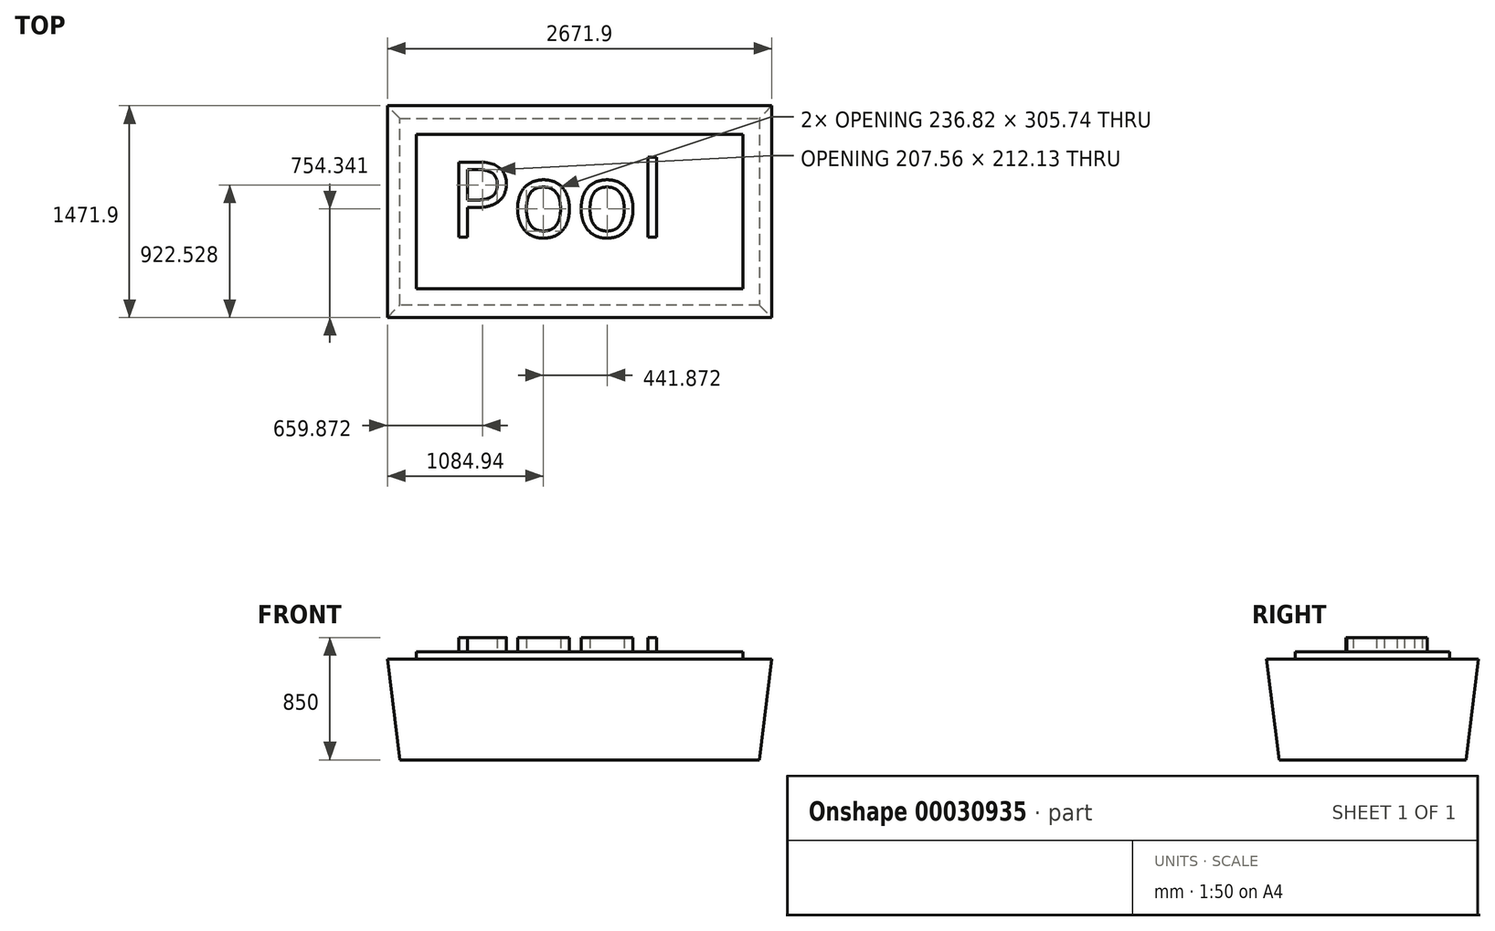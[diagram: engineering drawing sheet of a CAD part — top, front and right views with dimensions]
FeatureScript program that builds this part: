
annotation { "Feature Type Name" : "Feature", "Feature Type Description" : "" }
export const myFeature = defineFeature(function(context is Context, id is Id, definition is map)
    precondition{}
    {
        {
            var Q0;
            Q0=qCreatedBy(makeId("Top.planeOp"),FACE);
            var sketch = newSketch(context, id + "F0", { "sketchPlane" : qUnion([Q0])});
            skLineSegment(sketch, "E0.rect.bottom", {"start": v(-1250, 650) * mm, "end": v(1250, 650) * mm});
            skLineSegment(sketch, "E0.rect.top", {"start": v(-1250, -650) * mm, "end": v(1250, -650) * mm});
            skLineSegment(sketch, "E0.rect.left", {"start": v(-1250, 650) * mm, "end": v(-1250, -650) * mm});
            skLineSegment(sketch, "E0.rect.right", {"start": v(1250, 650) * mm, "end": v(1250, -650) * mm});
            skPoint(sketch, "E0.rect.middle", {"position": v(0, 0) * mm});
            skSolve(sketch);
        }
        {
            var Q0;
            Q0 = qSketchRegion(id + "F0", true);
            extrude(context, id + "F1", {"entities" : qUnion([Q0]), "depth" : 700 * mm, "hasDraft" : true, "draftAngle" : 7 * degree});
        }
        {
            var Q0;
            Q0=makeQuery(id+"F1.opExtrude","CAP_FACE",FACE,{"disambiguationData":[OSD([sQuery(id+"F0.wireOp",EDGE,"E0.rect.bottom"),sQuery(id+"F0.wireOp",EDGE,"E0.rect.top"),sQuery(id+"F0.wireOp",EDGE,"E0.rect.left"),sQuery(id+"F0.wireOp",EDGE,"E0.rect.right")])],"isStart":false});
            var sketch = newSketch(context, id + "F2", { "sketchPlane" : qUnion([Q0])});
            skLineSegment(sketch, "E1.rect.bottom", {"start": v(-1135.95, 535.95) * mm, "end": v(1135.95, 535.95) * mm});
            skLineSegment(sketch, "E1.rect.top", {"start": v(-1135.95, -535.95) * mm, "end": v(1135.95, -535.95) * mm});
            skLineSegment(sketch, "E1.rect.left", {"start": v(-1135.95, 535.95) * mm, "end": v(-1135.95, -535.95) * mm});
            skLineSegment(sketch, "E1.rect.right", {"start": v(1135.95, 535.95) * mm, "end": v(1135.95, -535.95) * mm});
            skPoint(sketch, "E1.rect.middle", {"position": v(0, 0) * mm});
            skSolve(sketch);
        }
        {
            var Q0;
            Q0 = qSketchRegion(id + "F2", true);
            extrude(context, id + "F3", {"entities" : qUnion([Q0]), "depth" : 50 * mm});
        }
        {
            var Q0;
            Q0=makeQuery(id+"F3.opExtrude","CAP_FACE",FACE,{"disambiguationData":[OSD([sQuery(id+"F2.wireOp",EDGE,"E1.rect.bottom"),sQuery(id+"F2.wireOp",EDGE,"E1.rect.top"),sQuery(id+"F2.wireOp",EDGE,"E1.rect.left"),sQuery(id+"F2.wireOp",EDGE,"E1.rect.right")])],"isStart":false});
            var sketch = newSketch(context, id + "F4", { "sketchPlane" : qUnion([Q0])});
            skText(sketch, "E2", { "text": "Pool", "fontName": "OpenSans-Regular.ttf"});
            const initialGuessF4  = {"E2": [-0.91233, -0.177, 1, 0, 0.52668]};
            skSetInitialGuess(sketch, initialGuessF4);
            skSolve(sketch);
        }
        {
            var Q0;
            Q0 = qSketchRegion(id + "F4", true);
            extrude(context, id + "F5", {"entities" : qUnion([Q0]), "depth" : 100 * mm});
        }
    });
